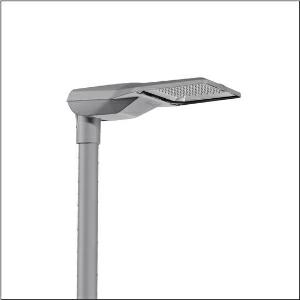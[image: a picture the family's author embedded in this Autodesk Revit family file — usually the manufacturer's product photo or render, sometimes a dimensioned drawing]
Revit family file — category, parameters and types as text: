
# Revit family: streetlight_sl_21_iq_midi___st1_5a_5xe3p31g08mb_98ff
name_source: partatom
category: Lighting Fixtures
units: mm (PartAtom-declared; Revit-internal decimal feet)

## family parameters
Cut with Voids When Loaded = No
Host = Face
Light Source = No
Part Type = Normal
Room Calculation Point = No
Round Connector Dimension = Use Diameter
Shared = No

## types (1)
- --- (1 x LED, 19170 lm, 146.7 W, 3000K)
    Apparent Load = 147 VA
    CIE Flux Codes = 22 53 95 100 100
    Color Rendering = 70
    Color Temperature = 3000K
    Default Elevation = 1800 mm
    Description = Streetlight SL 21 iQ midi, mast luminaire, primary light control with lens, of PMMA, primary optical cover: cover, of toughened safety glass, transparent, light distribution: ST1.5a, light emission: direct distribution, primary light characteristic: asymmetric, installation type: post-top, side-entry, LED, High Power LED, rated luminous flux: 19.170lm, luminous efficacy: 131lm/W, light colour: 730, colour temperature: 3000K, control: Street-Remote, Auto-Match, Temp-Guard, Lumen-Switch, Night-Set, Smart-Wire, Light-Fading, Desk-Remote (wireless, voltage-free reading and setting of iQ features in the workshop via application-optimized NFC function/RFID function), optimised constant luminous flux control (CLO 2.0), pre-setting: linear dimming characteristic, mains connection: 230..240V, AC, 50/60Hz, start of lifetime: 147W, end of service life: 161W, reduction: 62W, luminaire housing, of diecast aluminium, powder-coated, Siteco® metallic grey (DB 702S), corrosivity category C5 mid according to DIN EN ISO 12944, please order mast flange separately, inclination adjustable: 0°, 5°, 10°, 15°, sealing non-destructively replaceable, multi-level sealing system, length: 644mm, width: 335mm, height: 110mm, mast flange for spigot size: 42mm (side-entry): 5XC10008XM4, 60/48mm (side-entry/post-top): 5XC10108XM2, 76/60mm (side-entry/post-top): 5XC10108XM1, protection rating (complete): IP66, insulation class (complete): insulation class II (safety insulation), certification: CE, ENEC, ENEC+, VDE, impact resistance: IK09, permissible operating ambient temperature for outdoor applications: -40..+50°C, standard-compliant lighting for roads and squares, packaging unit: 1 piece

Light Distribution: ST1.5a
    Height = 111 mm
    Lamp = 1 x LED
    Lamp Light Flux = 19170 lm
    Lamp Power = 146.7 W
    Lamp count = 1
    Length = 644 mm
    Luminous efficacy = 131 lm/W
    Manufacturer = Siteco
    ModVariant = No
    Model = 5XE3P31G08MB
    Number of Poles = 1
    OnlyDefault = Yes
    Power Factor = 1
    Product Name = Streetlight SL 21 iQ midi | ST1.5a
    Product group = mast luminaire | pylon top
    ProductGroupID = 6100
    Protection Class = Protection class II
    Protection Degree = IP 66
    RLX_Detail_Level = 1
    RLX_Emergency_Light_Flux = 0 lm
    RLX_Emergency_Type = 0
    RLX_Emergency_Type_DB = No
    RlxData = <blob elided: 94085 chars, md5=da6172cc>
    Socket = socket
    Standby Power = 0 W
    System Light Flux = 19169 lm
    System Power = 147 W
    Type Comments = factory setting: luminous flux: 100 % | dim-lin: 254 | 753 mA
    Type Image = l_1004298.jpg
    URL = http://relux.com
    VarID = @adj_147551
    Voltage = 0 V
    Weight = 0.00 kg
    Width = 336 mm

## geometry (parser evidence)
native form markers: Blend x4, Sweep x9
no freeform markers — native parametric forms only
